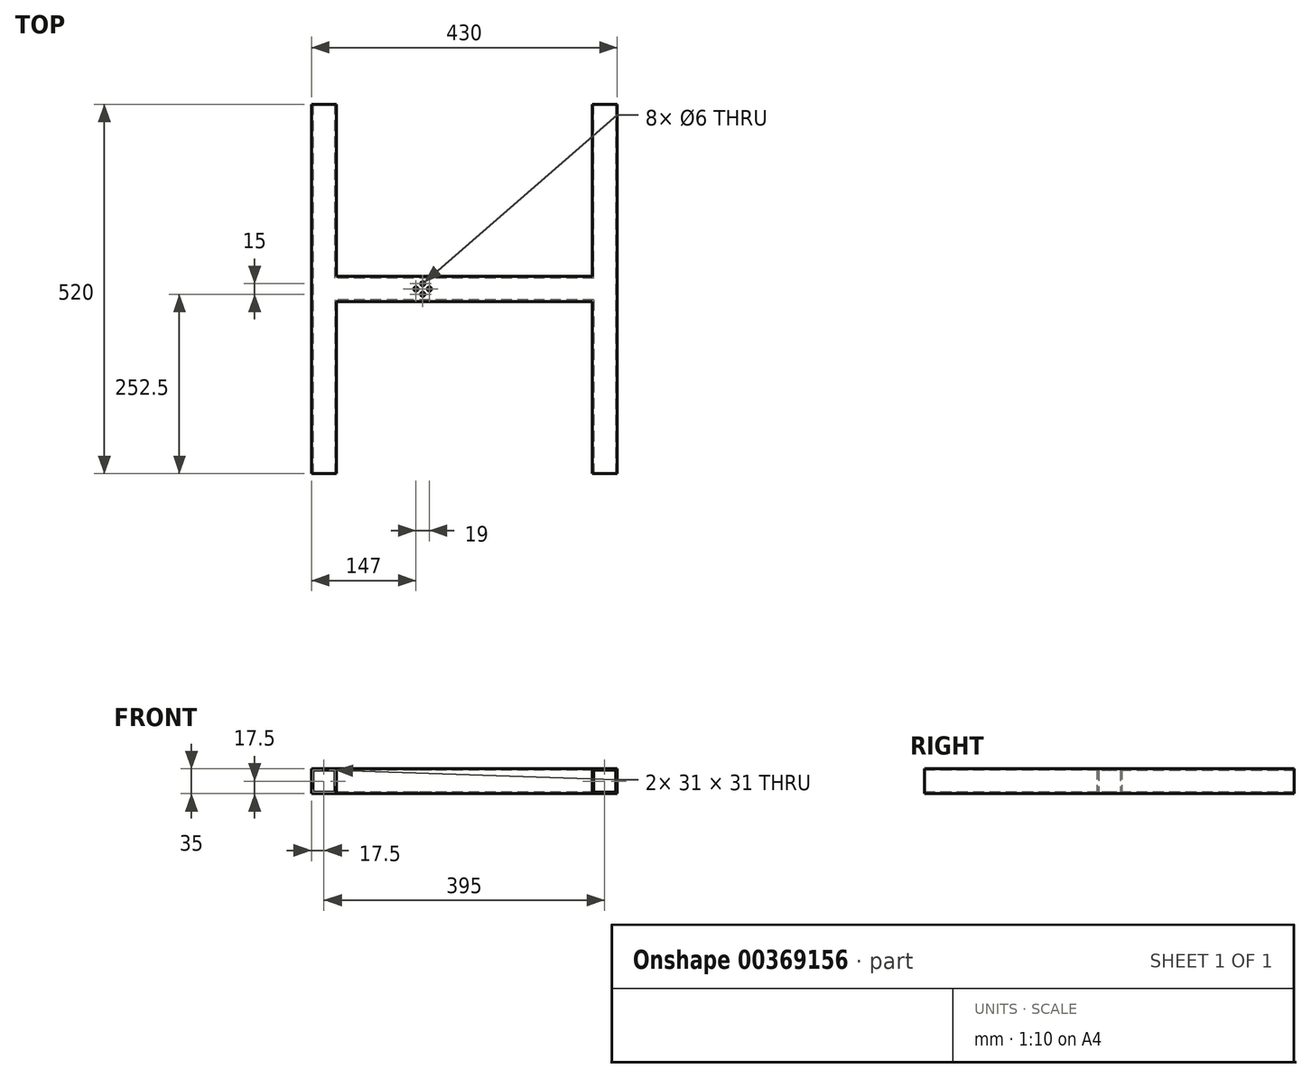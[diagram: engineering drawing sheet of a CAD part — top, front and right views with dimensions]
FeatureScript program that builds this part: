
annotation { "Feature Type Name" : "Feature", "Feature Type Description" : "" }
export const myFeature = defineFeature(function(context is Context, id is Id, definition is map)
    precondition{}
    {
        {
            var Q0;
            Q0=qCreatedBy(makeId("Top.planeOp"),FACE);
            var sketch = newSketch(context, id + "F0", { "sketchPlane" : qUnion([Q0])});
            skLineSegment(sketch, "E0", {"start": v(0, 17.5) * mm, "end": v(-180, 17.5) * mm});
            skLineSegment(sketch, "E1", {"start": v(-180, 17.5) * mm, "end": v(-180, 260) * mm});
            skLineSegment(sketch, "E2", {"start": v(-180, 260) * mm, "end": v(-215, 260) * mm});
            skLineSegment(sketch, "E3", {"start": v(-215, 260) * mm, "end": v(-215, 0) * mm});
            skLineSegment(sketch, "E4", {"start": v(-215, 0) * mm, "end": v(0, 0) * mm});
            skLineSegment(sketch, "E5", {"start": v(0, 0) * mm, "end": v(0, 17.5) * mm});
            skSolve(sketch);
        }
        {
            var Q0;
            Q0=makeQuery(id+"F0.imprint","IMPRINT",FACE,{"disambiguationData":[TD([[makeQuery(id+"F0.imprint","IMPRINT",EDGE,{"derivedFrom":sQuery(id+"F0.wireOp",EDGE,"E0")}),1.0]])]});
            extrude(context, id + "F1", {"entities" : qUnion([Q0]), "endBound" : BoundingType.SYMMETRIC, "depth" : 35 * mm});
        }
        {
            var Q0;
            Q0=makeQuery(id+"F1.opExtrude","SWEPT_BODY",BODY,{"disambiguationData":[OSD([sQuery(id+"F0.wireOp",EDGE,"E0"),sQuery(id+"F0.wireOp",EDGE,"E1"),sQuery(id+"F0.wireOp",EDGE,"E2"),sQuery(id+"F0.wireOp",EDGE,"E3"),sQuery(id+"F0.wireOp",EDGE,"E4"),sQuery(id+"F0.wireOp",EDGE,"E5")])]});
            var Q1;
            Q1=qCreatedBy(makeId("Front.planeOp"),FACE);
            mirror(context, id + "F2", {"operationType" : NewBodyOperationType.ADD, "entities" : qUnion([Q0]), "mirrorPlane" : qUnion([Q1])});
        }
        {
            var Q0;
            Q0=makeQuery(id+"F1.opExtrude","SWEPT_BODY",BODY,{"disambiguationData":[OSD([sQuery(id+"F0.wireOp",EDGE,"E0"),sQuery(id+"F0.wireOp",EDGE,"E1"),sQuery(id+"F0.wireOp",EDGE,"E2"),sQuery(id+"F0.wireOp",EDGE,"E3"),sQuery(id+"F0.wireOp",EDGE,"E4"),sQuery(id+"F0.wireOp",EDGE,"E5")])]});
            var Q1;
            Q1=qCreatedBy(makeId("Right.planeOp"),FACE);
            mirror(context, id + "F3", {"operationType" : NewBodyOperationType.ADD, "entities" : qUnion([Q0]), "mirrorPlane" : qUnion([Q1])});
        }
        {
            var Q0;
            Q0=makeQuery(id+"F2.opPattern","COPY",FACE,{"derivedFrom":makeQuery(id+"F1.opExtrude","SWEPT_FACE",FACE,{"disambiguationData":[OSD([sQuery(id+"F0.wireOp",EDGE,"E2")])]}),"instanceName":"1"});
            var Q1;
            Q1=makeQuery(id+"F3.opPattern","COPY",FACE,{"derivedFrom":makeQuery(id+"F2.opPattern","COPY",FACE,{"derivedFrom":makeQuery(id+"F1.opExtrude","SWEPT_FACE",FACE,{"disambiguationData":[OSD([sQuery(id+"F0.wireOp",EDGE,"E2")])]}),"instanceName":"1"}),"instanceName":"1"});
            var Q2;
            Q2=makeQuery(id+"F3.opPattern","COPY",FACE,{"derivedFrom":makeQuery(id+"F1.opExtrude","SWEPT_FACE",FACE,{"disambiguationData":[OSD([sQuery(id+"F0.wireOp",EDGE,"E2")])]}),"instanceName":"1"});
            var Q3;
            Q3=makeQuery(id+"F1.opExtrude","SWEPT_FACE",FACE,{"disambiguationData":[OSD([sQuery(id+"F0.wireOp",EDGE,"E2")])]});
            shell(context, id + "F4", {"entities" : qUnion([Q0, Q1, Q2, Q3]), "thickness" : 2 * mm});
        }
        {
            var Q0;
            {var subQ0=makeQuery(id+"F1.opExtrude","CAP_FACE",FACE,{"disambiguationData":[OSD([sQuery(id+"F0.wireOp",EDGE,"E0"),sQuery(id+"F0.wireOp",EDGE,"E1"),sQuery(id+"F0.wireOp",EDGE,"E2"),sQuery(id+"F0.wireOp",EDGE,"E3"),sQuery(id+"F0.wireOp",EDGE,"E4"),sQuery(id+"F0.wireOp",EDGE,"E5")])],"isStart":false});var subQ1=makeQuery(id+"F2.boolean.opBoolean","MERGE",FACE,{"derivedFrom":[subQ0,makeQuery(id+"F2.opPattern","COPY",FACE,{"derivedFrom":subQ0,"instanceName":"1"})]});Q0=makeQuery(id+"F3.boolean.opBoolean","MERGE",FACE,{"derivedFrom":[subQ1,makeQuery(id+"F3.opPattern","COPY",FACE,{"derivedFrom":subQ1,"instanceName":"1"})]});}
            var sketch = newSketch(context, id + "F5", { "sketchPlane" : qUnion([Q0])});
            skPoint(sketch, "E6", {"position": v(-49, 0) * mm});
            skPoint(sketch, "E7", {"position": v(-68, 0) * mm});
            skPoint(sketch, "E8", {"position": v(-58.5, 7.5) * mm});
            skPoint(sketch, "E9", {"position": v(-58.5, -7.5) * mm});
            skLineSegment(sketch, "E10", {"start": v(-58.5, 7.5) * mm, "end": v(-58.5, -7.5) * mm, "construction": true});
            skSolve(sketch);
        }
        {
            var Q0;
            Q0=sQuery(id+"F5.wireOp",VERTEX,"E7");
            var Q1;
            Q1=sQuery(id+"F5.wireOp",VERTEX,"E8");
            var Q2;
            Q2=sQuery(id+"F5.wireOp",VERTEX,"E6");
            var Q3;
            Q3=sQuery(id+"F5.wireOp",VERTEX,"E9");
            var Q4;
            Q4=makeQuery(id+"F1.opExtrude","SWEPT_BODY",BODY,{"disambiguationData":[OSD([sQuery(id+"F0.wireOp",EDGE,"E0"),sQuery(id+"F0.wireOp",EDGE,"E1"),sQuery(id+"F0.wireOp",EDGE,"E2"),sQuery(id+"F0.wireOp",EDGE,"E3"),sQuery(id+"F0.wireOp",EDGE,"E4"),sQuery(id+"F0.wireOp",EDGE,"E5")])]});
            hole(context, id + "F6", {"style" : HoleStyle.SIMPLE, "endStyle" : HoleEndStyle.THROUGH, "holeDiameter" : 6 * mm, "isTappedThrough" : true, "tappedDepth" : 12.7 * mm, "tapClearance" : 3, "locations" : qUnion([Q0, Q1, Q2, Q3]), "scope" : qUnion([Q4])});
        }
    });
